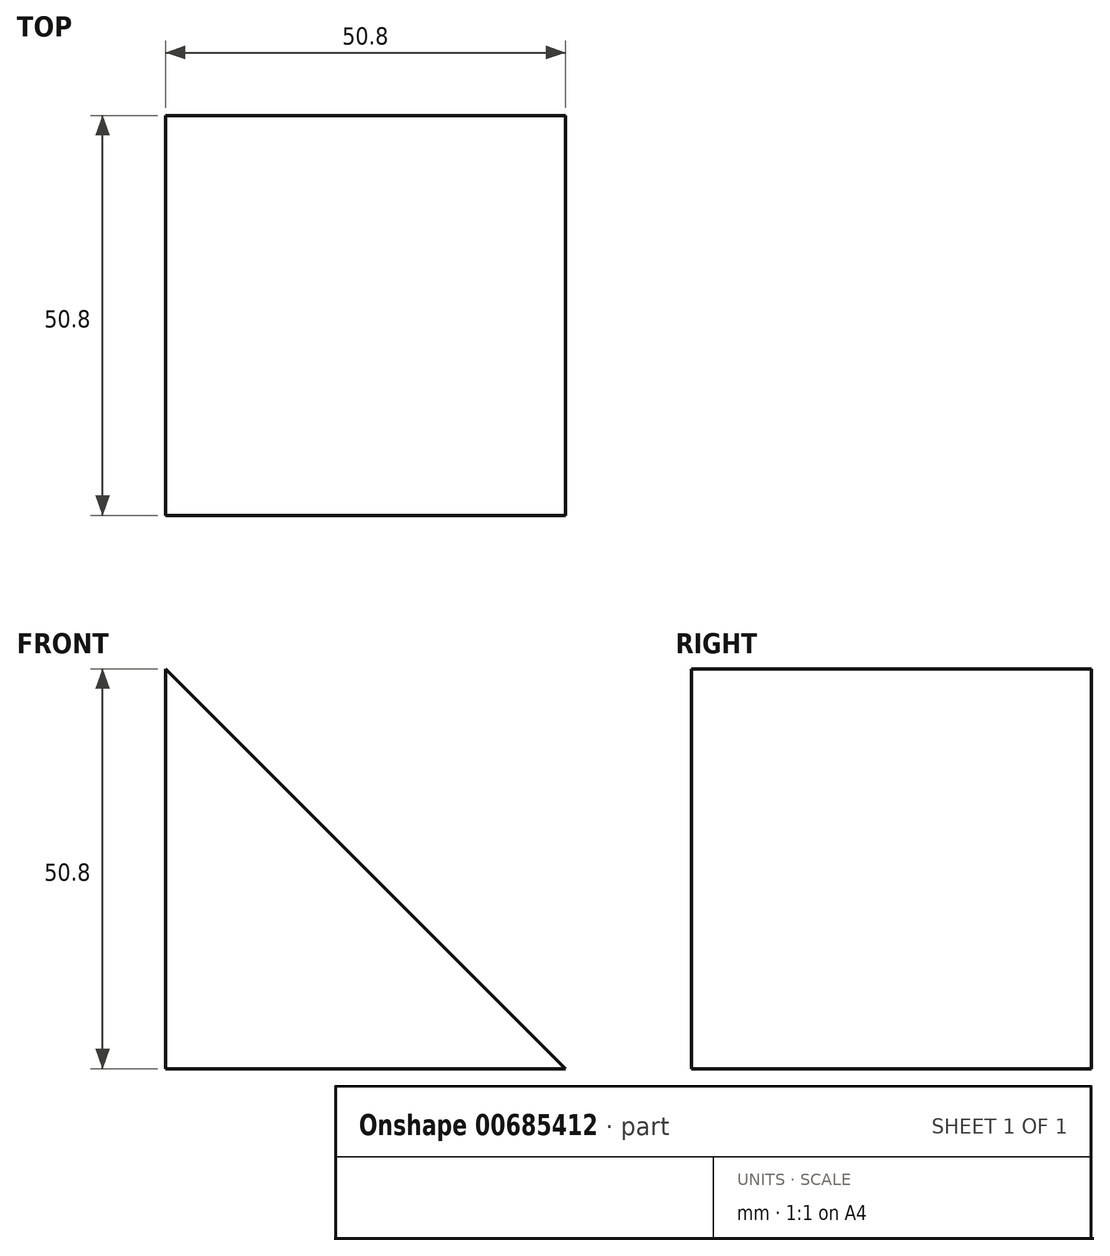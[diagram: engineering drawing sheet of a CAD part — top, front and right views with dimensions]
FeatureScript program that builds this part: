
annotation { "Feature Type Name" : "Feature", "Feature Type Description" : "" }
export const myFeature = defineFeature(function(context is Context, id is Id, definition is map)
    precondition{}
    {
        {
            var Q0;
            Q0=qCreatedBy(makeId("Front.planeOp"),FACE);
            var sketch = newSketch(context, id + "F0", { "sketchPlane" : qUnion([Q0])});
            skLineSegment(sketch, "E0", {"start": v(0, 0) * mm, "end": v(0, 50.8) * mm});
            skLineSegment(sketch, "E1", {"start": v(0, 50.8) * mm, "end": v(50.8, 0) * mm});
            skLineSegment(sketch, "E2", {"start": v(50.8, 0) * mm, "end": v(0, 0) * mm});
            skSolve(sketch);
        }
        {
            var Q0;
            Q0=makeQuery(id+"F0.imprint","IMPRINT",FACE,{"disambiguationData":[TD([[makeQuery(id+"F0.imprint","IMPRINT",EDGE,{"derivedFrom":sQuery(id+"F0.wireOp",EDGE,"E0")}),-1.0]])]});
            extrude(context, id + "F1", {"entities" : qUnion([Q0]), "depth" : 50.8 * mm, "offsetDistance" : 25.4 * mm});
        }
    });
